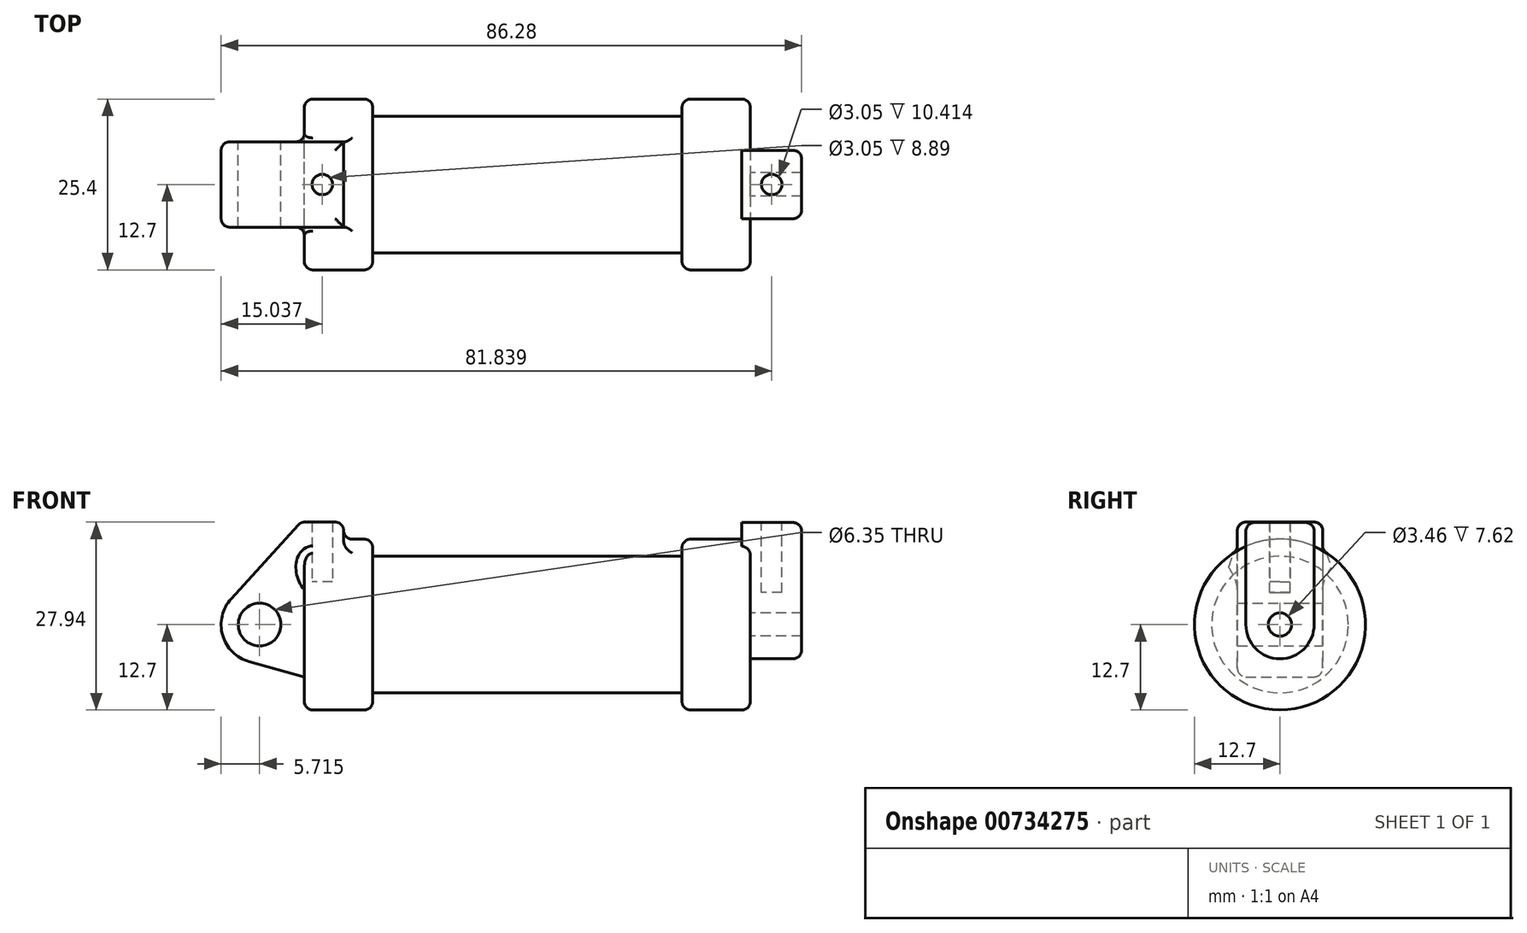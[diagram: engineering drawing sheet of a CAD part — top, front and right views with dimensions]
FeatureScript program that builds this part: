
annotation { "Feature Type Name" : "Feature", "Feature Type Description" : "" }
export const myFeature = defineFeature(function(context is Context, id is Id, definition is map)
    precondition{}
    {
        {
            var Q0;
            Q0=qCreatedBy(makeId("Front.planeOp"),FACE);
            var sketch = newSketch(context, id + "F0", { "sketchPlane" : qUnion([Q0])});
            skLineSegment(sketch, "E0", {"start": v(0, 0) * mm, "end": v(0, 12.7) * mm});
            skLineSegment(sketch, "E1", {"start": v(0, 12.7) * mm, "end": v(10.16, 12.7) * mm});
            skLineSegment(sketch, "E2", {"start": v(10.16, 12.7) * mm, "end": v(10.16, 10.16) * mm});
            skLineSegment(sketch, "E3", {"start": v(10.16, 10.16) * mm, "end": v(56.13, 10.16) * mm});
            skLineSegment(sketch, "E4", {"start": v(56.13, 10.16) * mm, "end": v(56.13, 12.7) * mm});
            skLineSegment(sketch, "E5", {"start": v(56.13, 12.7) * mm, "end": v(66.3, 12.7) * mm});
            skLineSegment(sketch, "E6", {"start": v(66.3, 12.7) * mm, "end": v(66.3, 0) * mm});
            skLineSegment(sketch, "E7", {"start": v(66.3, 0) * mm, "end": v(0, 0) * mm});
            skLineSegment(sketch, "E8", {"start": v(5.84, 15.24) * mm, "end": v(-0.5, 15.24) * mm});
            skLineSegment(sketch, "E9", {"start": v(-0.5, 15.24) * mm, "end": v(-10.88, 3.85) * mm});
            skLineSegment(sketch, "E10", {"start": v(0, 0) * mm, "end": v(-6.65, 0) * mm});
            skCircle(sketch, "E11", {"center": v(-6.65, 0) * mm, "radius": 5.72 * mm});
            skCircle(sketch, "E12", {"center": v(-6.65, 0) * mm, "radius": 3.18 * mm});
            skLineSegment(sketch, "E13", {"start": v(5.84, 15.24) * mm, "end": v(5.84, -9.4) * mm});
            skLineSegment(sketch, "E14", {"start": v(5.84, -9.4) * mm, "end": v(-8.18, -5.5) * mm});
            skSolve(sketch);
        }
        {
            var Q0;
            {var subQ0=sQuery(id+"F0.wireOp",EDGE,"E2");Q0=makeQuery(id+"F0.imprint","IMPRINT",FACE,{"disambiguationData":[TD([[makeQuery(id+"F0.imprint","IMPRINT",EDGE,{"derivedFrom":subQ0}),-1.0]])]});}
            var Q1;
            {var subQ0=sQuery(id+"F0.wireOp",EDGE,"E0");Q1=makeQuery(id+"F0.imprint","IMPRINT",FACE,{"disambiguationData":[TD([[makeQuery(id+"F0.imprint","IMPRINT",EDGE,{"derivedFrom":subQ0}),-1.0]])]});}
            var Q2;
            Q2=sQuery(id+"F0.wireOp",EDGE,"E7");
            revolve(context, id + "F1", {"surfaceOperationType" : NewSurfaceOperationType.NEW, "entities" : qUnion([Q0, Q1]), "axis" : qUnion([Q2]), "revolveType" : RevolveType.FULL});
        }
        {
            var Q0;
            {var subQ0=sQuery(id+"F0.wireOp",EDGE,"E0");Q0=makeQuery(id+"F0.imprint","IMPRINT",FACE,{"disambiguationData":[TD([[makeQuery(id+"F0.imprint","IMPRINT",EDGE,{"derivedFrom":subQ0}),-1.0]])]});}
            var Q1;
            {var subQ5=sQuery(id+"F0.wireOp",EDGE,"E12");Q1=makeQuery(id+"F0.imprint","IMPRINT",FACE,{"disambiguationData":[TD([[makeQuery(id+"F0.imprint","IMPRINT",EDGE,{"derivedFrom":subQ5}),-1.0]])]});}
            var Q2;
            {var subQ0=sQuery(id+"F0.wireOp",EDGE,"E14");Q2=makeQuery(id+"F0.imprint","IMPRINT",FACE,{"disambiguationData":[TD([[makeQuery(id+"F0.imprint","IMPRINT",EDGE,{"derivedFrom":subQ0}),-1.0]])]});}
            var Q3;
            {var subQ1=sQuery(id+"F0.wireOp",EDGE,"E0");Q3=makeQuery(id+"F0.imprint","IMPRINT",FACE,{"disambiguationData":[TD([[makeQuery(id+"F0.imprint","IMPRINT",EDGE,{"derivedFrom":subQ1}),1.0]])]});}
            extrude(context, id + "F2", {"entities" : qUnion([Q0, Q1, Q2, Q3]), "operationType" : NewBodyOperationType.ADD, "depth" : 6.35 * mm, "offsetDistance" : 25.4 * mm, "hasSecondDirection" : true, "secondDirectionOppositeDirection" : true, "secondDirectionDepth" : 6.35 * mm});
        }
        {
            var Q0;
            Q0=makeQuery(id+"F1.opRevolve","SWEPT_FACE",FACE,{"disambiguationData":[OSD([sQuery(id+"F0.wireOp",EDGE,"E6")])]});
            var sketch = newSketch(context, id + "F3", { "sketchPlane" : qUnion([Q0])});
            skCircle(sketch, "E15", {"center": v(0, 0) * mm, "radius": 1.73 * mm});
            skCircle(sketch, "E16", {"center": v(0, 0) * mm, "radius": 5.08 * mm});
            skLineSegment(sketch, "E17", {"start": v(-5.08, 0) * mm, "end": v(-5.08, 15.16) * mm});
            skLineSegment(sketch, "E18", {"start": v(5.08, 0) * mm, "end": v(5.08, 15.16) * mm});
            skLineSegment(sketch, "E19", {"start": v(-5.08, 15.16) * mm, "end": v(5.08, 15.16) * mm});
            skSolve(sketch);
        }
        {
            var Q0;
            {var subQ0=sQuery(id+"F3.wireOp",EDGE,"E17");var subQ1=sQuery(id+"F3.wireOp",EDGE,"E16");var subQ2=makeQuery(id+"F3.imprint","INTERSECT",VERTEX,{"derivedFrom":[subQ1,subQ0]});Q0=makeQuery(id+"F3.imprint","IMPRINT",FACE,{"disambiguationData":[TD([[makeQuery(id+"F3.imprint","IMPRINT",EDGE,{"disambiguationData":[TD([[subQ2,1.0]])],"derivedFrom":subQ1}),-1.0]])]});}
            var Q1;
            {var subQ0=sQuery(id+"F3.wireOp",EDGE,"E19");Q1=makeQuery(id+"F3.imprint","IMPRINT",FACE,{"disambiguationData":[TD([[makeQuery(id+"F3.imprint","IMPRINT",EDGE,{"derivedFrom":subQ0}),-1.0]])]});}
            var Q2;
            Q2=makeQuery(id+"F3.imprint","IMPRINT",FACE,{"disambiguationData":[TD([[makeQuery(id+"F3.imprint","IMPRINT",EDGE,{"derivedFrom":sQuery(id+"F3.wireOp",EDGE,"E15")}),-1.0]])]});
            extrude(context, id + "F4", {"entities" : qUnion([Q0, Q1, Q2]), "operationType" : NewBodyOperationType.ADD, "depth" : 7.62 * mm, "offsetDistance" : 25.4 * mm, "hasSecondDirection" : true, "secondDirectionOppositeDirection" : true, "secondDirectionDepth" : 1.27 * mm});
        }
        {
            var Q0;
            Q0=makeQuery(id+"F4.opExtrude","SWEPT_FACE",FACE,{"disambiguationData":[OSD([sQuery(id+"F3.wireOp",EDGE,"E19")])]});
            var sketch = newSketch(context, id + "F5", { "sketchPlane" : qUnion([Q0])});
            skCircle(sketch, "E20", {"center": v(69.47, 0) * mm, "radius": 1.52 * mm});
            skPoint(sketch, "E20.centerSnap0", {"position": v(65.02, 0) * mm});
            skPoint(sketch, "E20.centerSnap1", {"position": v(69.47, -5.08) * mm});
            skSolve(sketch);
        }
        {
            var Q0;
            Q0=makeQuery(id+"F5.imprint","IMPRINT",FACE,{"disambiguationData":[TD([[makeQuery(id+"F5.imprint","IMPRINT",EDGE,{"derivedFrom":sQuery(id+"F5.wireOp",EDGE,"E20")}),1.0]])]});
            extrude(context, id + "F6", {"entities" : qUnion([Q0]), "operationType" : NewBodyOperationType.REMOVE, "oppositeDirection" : true, "depth" : 10.4 * mm, "offsetDistance" : 25.4 * mm});
        }
        {
            var Q0;
            Q0=makeQuery(id+"F2.opExtrude","SWEPT_FACE",FACE,{"disambiguationData":[OSD([sQuery(id+"F0.wireOp",EDGE,"E8")])]});
            var sketch = newSketch(context, id + "F7", { "sketchPlane" : qUnion([Q0])});
            skCircle(sketch, "E21", {"center": v(2.67, 0) * mm, "radius": 1.52 * mm});
            skPoint(sketch, "E21.centerSnap0", {"position": v(2.67, 6.35) * mm});
            skPoint(sketch, "E21.centerSnap1", {"position": v(-0.5, 0) * mm});
            skSolve(sketch);
        }
        {
            var Q0;
            Q0=makeQuery(id+"F7.imprint","IMPRINT",FACE,{"disambiguationData":[TD([[makeQuery(id+"F7.imprint","IMPRINT",EDGE,{"derivedFrom":sQuery(id+"F7.wireOp",EDGE,"E21")}),1.0]])]});
            extrude(context, id + "F8", {"entities" : qUnion([Q0]), "operationType" : NewBodyOperationType.REMOVE, "endBound" : BoundingType.SYMMETRIC, "depth" : 17.78 * mm, "offsetDistance" : 25.4 * mm});
        }
        {
            var Q0;
            Q0=makeQuery(id+"F1.opRevolve","SWEPT_EDGE",EDGE,{"disambiguationData":[OSD([sQuery(id+"F0.wireOp",EDGE,"E0"),sQuery(id+"F0.wireOp",EDGE,"E1")])]});
            var Q1;
            Q1=makeQuery(id+"F1.opRevolve","SWEPT_EDGE",EDGE,{"disambiguationData":[OSD([sQuery(id+"F0.wireOp",EDGE,"E1"),sQuery(id+"F0.wireOp",EDGE,"E2")])]});
            var Q2;
            Q2=makeQuery(id+"F1.opRevolve","SWEPT_FACE",FACE,{"disambiguationData":[OSD([sQuery(id+"F0.wireOp",EDGE,"E1")])]});
            var Q3;
            Q3=makeQuery(id+"F2.opExtrude","CAP_EDGE",EDGE,{"disambiguationData":[OSD([sQuery(id+"F0.wireOp",EDGE,"E9")])],"isStart":true});
            var Q4;
            Q4=makeQuery(id+"F2.opExtrude","CAP_EDGE",EDGE,{"disambiguationData":[OSD([sQuery(id+"F0.wireOp",EDGE,"E9")])],"isStart":false});
            var Q5;
            Q5=makeQuery(id+"F1.opRevolve","SWEPT_EDGE",EDGE,{"disambiguationData":[OSD([sQuery(id+"F0.wireOp",EDGE,"E4"),sQuery(id+"F0.wireOp",EDGE,"E5")])]});
            var Q6;
            Q6=makeQuery(id+"F1.opRevolve","SWEPT_EDGE",EDGE,{"disambiguationData":[OSD([sQuery(id+"F0.wireOp",EDGE,"E5"),sQuery(id+"F0.wireOp",EDGE,"E6")])]});
            var Q7;
            Q7=makeQuery(id+"F4.opExtrude","SWEPT_EDGE",EDGE,{"disambiguationData":[OSD([sQuery(id+"F3.wireOp",EDGE,"E17"),sQuery(id+"F3.wireOp",EDGE,"E19")])]});
            var Q8;
            Q8=makeQuery(id+"F4.opExtrude","SWEPT_EDGE",EDGE,{"disambiguationData":[OSD([sQuery(id+"F3.wireOp",EDGE,"E18"),sQuery(id+"F3.wireOp",EDGE,"E19")])]});
            var Q9;
            Q9=makeQuery(id+"F4.opExtrude","CAP_EDGE",EDGE,{"disambiguationData":[OSD([sQuery(id+"F3.wireOp",EDGE,"E19")])],"isStart":false});
            var Q10;
            Q10=makeQuery(id+"F4.opExtrude","CAP_EDGE",EDGE,{"disambiguationData":[OSD([sQuery(id+"F3.wireOp",EDGE,"E17")])],"isStart":false});
            var Q11;
            Q11=makeQuery(id+"F2.opExtrude","SWEPT_EDGE",EDGE,{"disambiguationData":[OSD([sQuery(id+"F0.wireOp",EDGE,"E8"),sQuery(id+"F0.wireOp",EDGE,"E13")])]});
            var Q12;
            Q12=makeQuery(id+"F2.opExtrude","CAP_EDGE",EDGE,{"disambiguationData":[OSD([sQuery(id+"F0.wireOp",EDGE,"E8")])],"isStart":true});
            var Q13;
            Q13=makeQuery(id+"F2.opExtrude","CAP_EDGE",EDGE,{"disambiguationData":[OSD([sQuery(id+"F0.wireOp",EDGE,"E8")])],"isStart":false});
            var Q14;
            Q14=makeQuery(id+"F2.opExtrude","SWEPT_EDGE",EDGE,{"disambiguationData":[OSD([sQuery(id+"F0.wireOp",EDGE,"E8"),sQuery(id+"F0.wireOp",EDGE,"E9")])]});
            fillet(context, id + "F9", {"entities" : qUnion([Q0, Q1, Q2, Q3, Q4, Q5, Q6, Q7, Q8, Q9, Q10, Q11, Q12, Q13, Q14]), "radius" : 1.27 * mm, "tangentPropagation" : true, "allowEdgeOverflow" : false});
        }
    });
